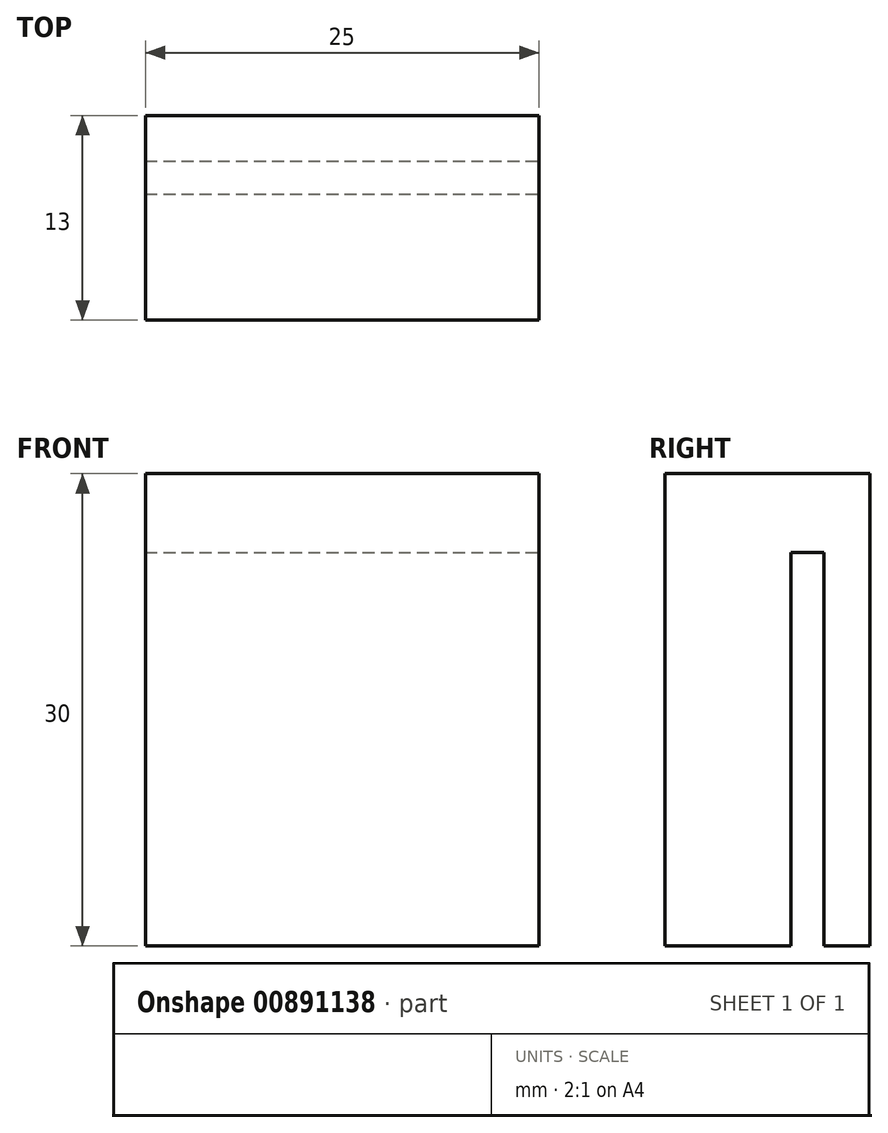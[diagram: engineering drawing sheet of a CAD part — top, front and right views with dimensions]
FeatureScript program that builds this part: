
annotation { "Feature Type Name" : "Feature", "Feature Type Description" : "" }
export const myFeature = defineFeature(function(context is Context, id is Id, definition is map)
    precondition{}
    {
        {
            var Q0;
            Q0=qCreatedBy(makeId("Front.planeOp"),FACE);
            var sketch = newSketch(context, id + "F0", { "sketchPlane" : qUnion([Q0])});
            skLineSegment(sketch, "E0.bottom", {"start": v(-12.5, -15) * mm, "end": v(12.5, -15) * mm});
            skLineSegment(sketch, "E0.top", {"start": v(-12.5, 15) * mm, "end": v(12.5, 15) * mm});
            skLineSegment(sketch, "E0.left", {"start": v(-12.5, -15) * mm, "end": v(-12.5, 15) * mm});
            skLineSegment(sketch, "E0.right", {"start": v(12.5, -15) * mm, "end": v(12.5, 15) * mm});
            skPoint(sketch, "E0.middle", {"position": v(0, 0) * mm});
            skSolve(sketch);
        }
        {
            var Q0;
            Q0 = qSketchRegion(id + "F0", true);
            extrude(context, id + "F1", {"entities" : qUnion([Q0]), "endBound" : BoundingType.SYMMETRIC, "depth" : 13 * mm, "offsetDistance" : 25 * mm});
        }
        {
            var Q0;
            Q0=makeQuery(id+"F1.opExtrude","SWEPT_FACE",FACE,{"disambiguationData":[OSD([sQuery(id+"F0.wireOp",EDGE,"E0.bottom")])]});
            var sketch = newSketch(context, id + "F2", { "sketchPlane" : qUnion([Q0])});
            skLineSegment(sketch, "E1.bottom", {"start": v(-12.5, -1.5) * mm, "end": v(12.5, -1.5) * mm});
            skLineSegment(sketch, "E1.top", {"start": v(-12.5, -3.6) * mm, "end": v(12.5, -3.6) * mm});
            skLineSegment(sketch, "E1.left", {"start": v(-12.5, -1.5) * mm, "end": v(-12.5, -3.6) * mm});
            skLineSegment(sketch, "E1.right", {"start": v(12.5, -1.5) * mm, "end": v(12.5, -3.6) * mm});
            skSolve(sketch);
        }
        {
            var Q0;
            Q0 = qSketchRegion(id + "F2", true);
            extrude(context, id + "F3", {"entities" : qUnion([Q0]), "operationType" : NewBodyOperationType.REMOVE, "oppositeDirection" : true, "depth" : 25 * mm, "offsetDistance" : 25 * mm});
        }
    });
